# Revit family: Absperrventil 4215 W IG-AG
name_source: partatom
category: Rohrzubehör
units: mm (PartAtom-declared; Revit-internal decimal feet)

## family parameters
Arbeitsebenenbasiert = Nein
Beim Laden mit Abzugskörper schneiden = Nein
Bemaßung runder Anschluss = Durchmesser verwenden
Gemeinsam genutzt = Nein
Immer vertikal = Ja
OmniClass-Nummer = 23.65.55.14
OmniClass-Titel = Valves for Liquid Services
Teiletyp = Unterbricht

## types (1)
- Absperrventil 4215 W IG-AG
    Anwendungsgebiet = Zum Absperren von Trinkwasserleitungen und -anlagen in Gebäuden
    Bestellnummer = 2412561
    Gehäuse = entzinkungsbeständiges Messing nach EN1982
    H01 = 26 mm  [stored 0.0853018 ft]
    H02 = 5 mm  [stored 0.0164042 ft]
    H03 = 15 mm  [stored 0.0492126 ft]
    H04 = 21 mm  [stored 0.0688976 ft]
    Handrad = Kunststoff, grün
    Hersteller = HERZ Armaturen Ges.m.b.H
    Hinweis = Gemäß Art 33 der REACH-Verordnung (EG Nr. 1907/2006) sind wir verpflichtet, darauf hinzuweisen, dass der Stoff Blei auf der SVHC-Liste geführt wird und dass alle aus Messing bestehenden Bauteile, die in unseren Erzeugnissen verarbeitet sind, mehr als 0,1 % (w/w) Blei (CAS: 7439-92-1 / EINECS: 231-100-4) enthalten.
Da Blei als Legierungsbestandteil fest gebunden ist, sind keine Expositionen zu erwarten und daher sind keine zusätzlichen Angaben zur sicheren Verwendung notwendig.
    L00 = 30 mm  [stored 0.0984252 ft]
    L01 = 13 mm
    L02 = 12 mm  [stored 0.0393701 ft]
    L03 = 17 mm  [stored 0.0557743 ft]
    L04 = 38 mm  [stored 0.124672 ft]
    L05 = 9 mm
    L06 = 18 mm  [stored 0.0590551 ft]
    Max. Betriebsdruck = 1000000.0 Pa
    Max. Betriebstemperatur = 90 °C
    Max. Differenzdruck auf geschlossenen Sitz = 1000000.0 Pa
    Medium = Trinkwasser
    O-Ringe = EPDM
    R01 = 16 mm  [stored 0.0524934 ft]
    R03 = 15 mm  [stored 0.0492126 ft]
    R07 = 3 mm  [stored 0.00984252 ft]
    S03 = 60 mm  [stored 0.19685 ft]
    SCTWCODE = 04;01;02
    SCTWSEQ = FW;SBT_TYP_FW="106";2
    SC_NennweiteBerechnet = 0
    T01 = 18 mm  [stored 0.0590551 ft]
    URL = www.herz-armaturen.at
    Vorgabe-Ansicht = 0 mm  [stored 0 ft]

note: [stored X ft] marks values corroborated as IEEE doubles in the binary element streams (Revit-internal decimal feet)
